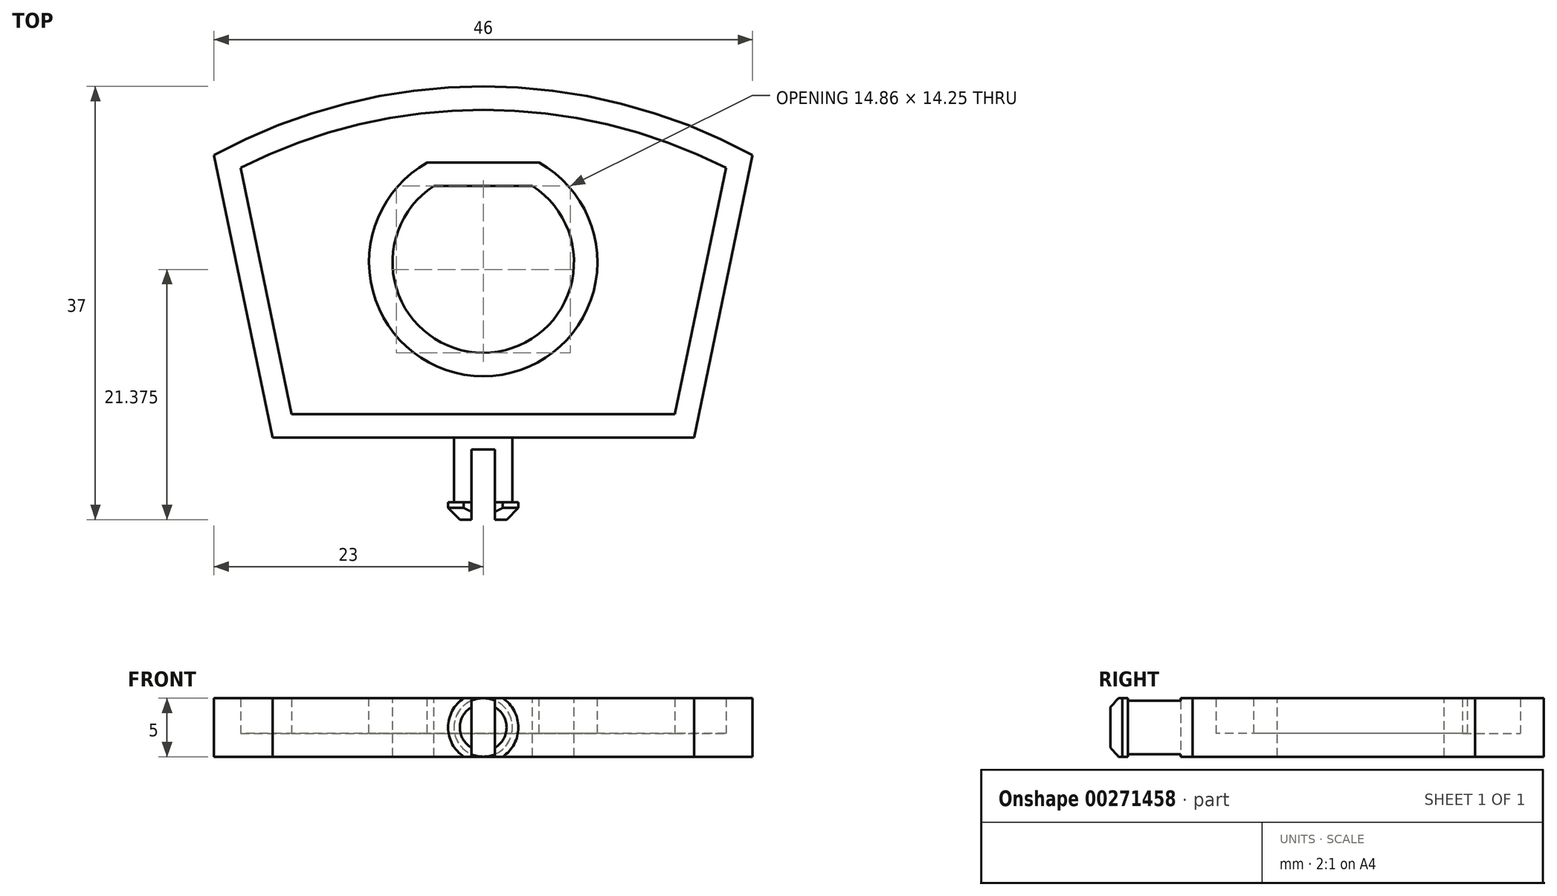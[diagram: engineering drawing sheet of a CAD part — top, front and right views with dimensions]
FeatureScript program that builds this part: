
annotation { "Feature Type Name" : "Feature", "Feature Type Description" : "" }
export const myFeature = defineFeature(function(context is Context, id is Id, definition is map)
    precondition{}
    {
        {
            var Q0;
            Q0=qCreatedBy(makeId("Top.planeOp"),FACE);
            var sketch = newSketch(context, id + "F0", { "sketchPlane" : qUnion([Q0])});
            skLineSegment(sketch, "E0", {"start": v(-23, 24.13) * mm, "end": v(-18, 0) * mm});
            skLineSegment(sketch, "E1", {"start": v(-18, 0) * mm, "end": v(18, 0) * mm});
            skLineSegment(sketch, "E2", {"start": v(18, 0) * mm, "end": v(23, 24.13) * mm});
            skArc(sketch, "E3", {"start": v(23, 24.13) * mm, "mid": v(0, 30) * mm, "end": v(-23, 24.13) * mm});
            skSolve(sketch);
        }
        {
            var Q0;
            Q0 = qSketchRegion(id + "F0", true);
            extrude(context, id + "F1", {"entities" : qUnion([Q0]), "depth" : 5 * mm, "symmetric" : true});
        }
        {
            var Q0;
            Q0=makeQuery(id+"F1.opExtrude","CAP_FACE",FACE,{"disambiguationData":[OSD([sQuery(id+"F0.wireOp",EDGE,"E0"),sQuery(id+"F0.wireOp",EDGE,"E1"),sQuery(id+"F0.wireOp",EDGE,"E2"),sQuery(id+"F0.wireOp",EDGE,"E3")])],"isStart":false});
            var sketch = newSketch(context, id + "F2", { "sketchPlane" : qUnion([Q0])});
            skLineSegment(sketch, "E4", {"start": v(-4.22, 21.5) * mm, "end": v(4.22, 21.5) * mm});
            skArc(sketch, "E5", {"start": v(-4.22, 21.5) * mm, "mid": v(0, 7.25) * mm, "end": v(4.22, 21.5) * mm});
            skSolve(sketch);
        }
        {
            var Q0;
            Q0 = qSketchRegion(id + "F2", true);
            extrude(context, id + "F3", {"entities" : qUnion([Q0]), "operationType" : NewBodyOperationType.REMOVE, "endBound" : BoundingType.UP_TO_NEXT, "oppositeDirection" : true, "depth" : 25 * mm});
        }
        {
            var Q0;
            Q0=makeQuery(id+"F1.opExtrude","CAP_FACE",FACE,{"disambiguationData":[OSD([sQuery(id+"F0.wireOp",EDGE,"E0"),sQuery(id+"F0.wireOp",EDGE,"E1"),sQuery(id+"F0.wireOp",EDGE,"E2"),sQuery(id+"F0.wireOp",EDGE,"E3")])],"isStart":false});
            shell(context, id + "F4", {"entities" : qUnion([Q0]), "thickness" : 2 * mm});
        }
        {
            var Q0;
            Q0=qCreatedBy(makeId("Right.planeOp"),FACE);
            var sketch = newSketch(context, id + "F5", { "sketchPlane" : qUnion([Q0])});
            skLineSegment(sketch, "E6", {"start": v(0, 0) * mm, "end": v(-7, 0) * mm});
            skLineSegment(sketch, "E7", {"start": v(-7, 0) * mm, "end": v(-7, 3) * mm});
            skLineSegment(sketch, "E8", {"start": v(-7, 3) * mm, "end": v(-5.5, 3) * mm});
            skLineSegment(sketch, "E9", {"start": v(-5.5, 3) * mm, "end": v(-5.5, 2.5) * mm});
            skLineSegment(sketch, "E10", {"start": v(-5.5, 2.5) * mm, "end": v(0, 2.5) * mm});
            skLineSegment(sketch, "E11", {"start": v(0, 2.5) * mm, "end": v(0, 0) * mm});
            skSolve(sketch);
        }
        {
            var Q0;
            Q0 = qSketchRegion(id + "F5", true);
            var Q1;
            Q1=sQuery(id+"F5.wireOp",EDGE,"E6");
            revolve(context, id + "F6", {"operationType" : NewBodyOperationType.ADD, "entities" : qUnion([Q0]), "axis" : qUnion([Q1]), "revolveType" : RevolveType.FULL});
        }
        {
            var Q0;
            Q0=makeQuery(id+"F6.opRevolve","SWEPT_EDGE",EDGE,{"disambiguationData":[OSD([sQuery(id+"F5.wireOp",EDGE,"E7"),sQuery(id+"F5.wireOp",EDGE,"E8")])]});
            chamfer(context, id + "F7", {"entities" : qUnion([Q0]), "width" : 1 * mm, "tangentPropagation" : true});
        }
        {
            var Q0;
            Q0=makeQuery(id+"F6.opRevolve","SWEPT_FACE",FACE,{"disambiguationData":[OSD([sQuery(id+"F5.wireOp",EDGE,"E7")])]});
            var sketch = newSketch(context, id + "F8", { "sketchPlane" : qUnion([Q0])});
            skLineSegment(sketch, "E12.bottom", {"start": v(-25.33, 2.5) * mm, "end": v(24.67, 2.5) * mm});
            skLineSegment(sketch, "E12.top", {"start": v(-25.33, -2.5) * mm, "end": v(24.67, -2.5) * mm});
            skLineSegment(sketch, "E12.left", {"start": v(-25.33, 2.5) * mm, "end": v(-25.33, -2.5) * mm});
            skLineSegment(sketch, "E12.right", {"start": v(24.67, 2.5) * mm, "end": v(24.67, -2.5) * mm});
            skSolve(sketch);
        }
        {
            var Q0;
            Q0 = qSketchRegion(id + "F8", true);
            extrude(context, id + "F9", {"entities" : qUnion([Q0]), "operationType" : NewBodyOperationType.INTERSECT, "endBound" : BoundingType.THROUGH_ALL, "oppositeDirection" : true, "depth" : 25 * mm});
        }
        {
            var Q0;
            Q0=makeQuery(id+"F6.opRevolve","SWEPT_FACE",FACE,{"disambiguationData":[OSD([sQuery(id+"F5.wireOp",EDGE,"E7")])]});
            var sketch = newSketch(context, id + "F10", { "sketchPlane" : qUnion([Q0])});
            skLineSegment(sketch, "E13.bottom", {"start": v(-1, 4.04) * mm, "end": v(1, 4.04) * mm});
            skLineSegment(sketch, "E13.top", {"start": v(-1, -4.2) * mm, "end": v(1, -4.2) * mm});
            skLineSegment(sketch, "E13.left", {"start": v(-1, 4.04) * mm, "end": v(-1, -4.2) * mm});
            skLineSegment(sketch, "E13.right", {"start": v(1, 4.04) * mm, "end": v(1, -4.2) * mm});
            skSolve(sketch);
        }
        {
            var Q0;
            Q0 = qSketchRegion(id + "F10", true);
            extrude(context, id + "F11", {"entities" : qUnion([Q0]), "operationType" : NewBodyOperationType.REMOVE, "oppositeDirection" : true, "depth" : 6 * mm});
        }
    });
